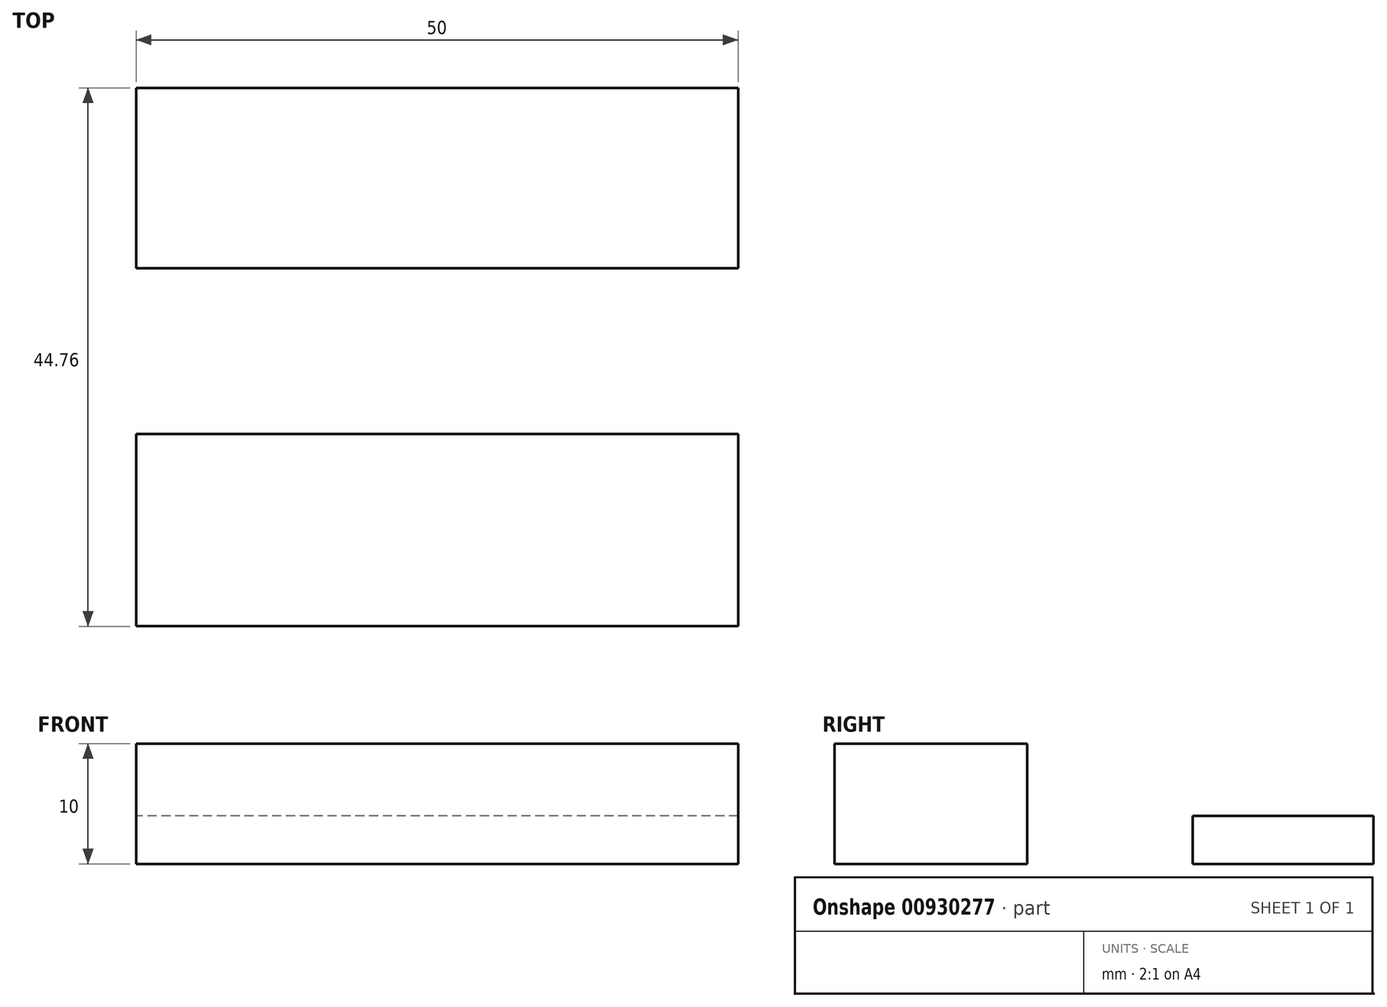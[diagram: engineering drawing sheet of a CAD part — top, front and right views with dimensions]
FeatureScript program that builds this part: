
annotation { "Feature Type Name" : "Feature", "Feature Type Description" : "" }
export const myFeature = defineFeature(function(context is Context, id is Id, definition is map)
    precondition{}
    {
        {
            var Q0;
            Q0=qCreatedBy(makeId("Top.planeOp"),FACE);
            var sketch = newSketch(context, id + "F0", { "sketchPlane" : qUnion([Q0])});
            skLineSegment(sketch, "E0.bottom", {"start": v(25, 7.5) * mm, "end": v(-25, 7.5) * mm});
            skLineSegment(sketch, "E0.top", {"start": v(25, -7.5) * mm, "end": v(-25, -7.5) * mm});
            skLineSegment(sketch, "E0.left", {"start": v(25, 7.5) * mm, "end": v(25, -7.5) * mm});
            skLineSegment(sketch, "E0.right", {"start": v(-25, 7.5) * mm, "end": v(-25, -7.5) * mm});
            skPoint(sketch, "E0.middle", {"position": v(0, 0) * mm});
            skSolve(sketch);
        }
        {
            var Q0;
            Q0 = qSketchRegion(id + "F0", true);
            var Q1;
            Q1=makeQuery(id+"F0.imprint","IMPRINT",FACE,{"disambiguationData":[TD([[makeQuery(id+"F0.imprint","IMPRINT",EDGE,{"derivedFrom":sQuery(id+"F0.wireOp",EDGE,"E0.bottom")}),1.0]])]});
            extrude(context, id + "F1", {"entities" : qUnion([Q0, Q1]), "depth" : 4 * mm, "offsetDistance" : 25 * mm});
        }
        {
            var Q0;
            Q0=qCreatedBy(makeId("Top.planeOp"),FACE);
            var sketch = newSketch(context, id + "F2", { "sketchPlane" : qUnion([Q0])});
            skLineSegment(sketch, "E1.bottom", {"start": v(25, -21.26) * mm, "end": v(-25, -21.26) * mm});
            skLineSegment(sketch, "E1.top", {"start": v(25, -37.26) * mm, "end": v(-25, -37.26) * mm});
            skLineSegment(sketch, "E1.left", {"start": v(25, -21.26) * mm, "end": v(25, -37.26) * mm});
            skLineSegment(sketch, "E1.right", {"start": v(-25, -21.26) * mm, "end": v(-25, -37.26) * mm});
            skPoint(sketch, "E1.middle", {"position": v(0, -29.26) * mm});
            skSolve(sketch);
        }
        {
            var Q0;
            Q0 = qSketchRegion(id + "F2", true);
            extrude(context, id + "F3", {"entities" : qUnion([Q0]), "depth" : 10 * mm, "offsetDistance" : 25 * mm});
        }
    });
